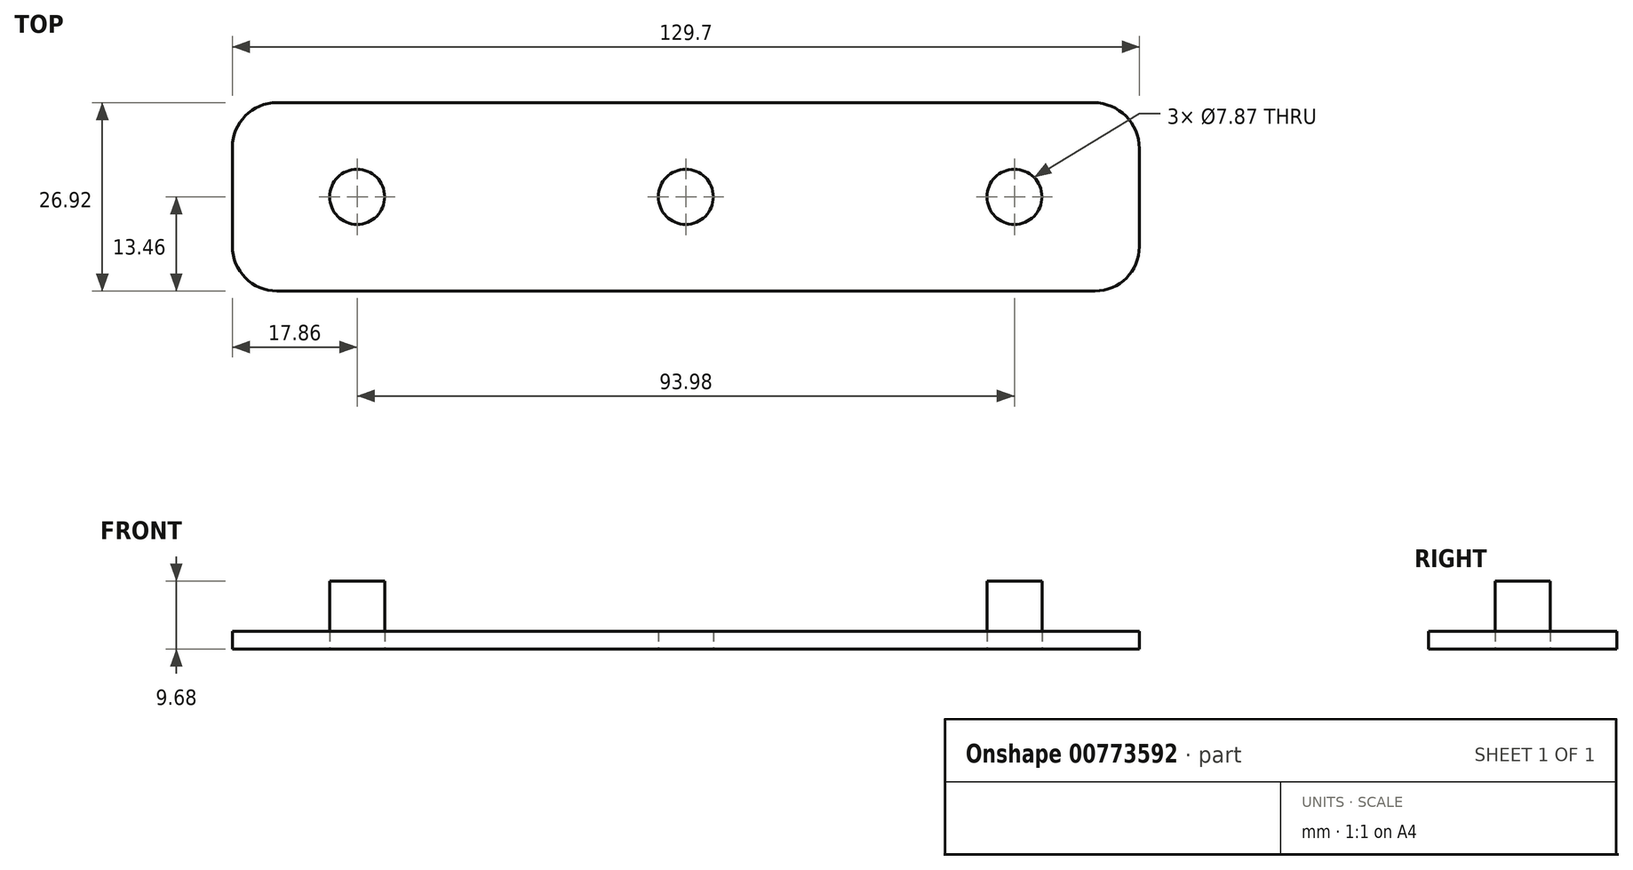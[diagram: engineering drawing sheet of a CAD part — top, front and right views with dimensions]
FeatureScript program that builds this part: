
annotation { "Feature Type Name" : "Feature", "Feature Type Description" : "" }
export const myFeature = defineFeature(function(context is Context, id is Id, definition is map)
    precondition{}
    {
        {
            var Q0;
            Q0=qCreatedBy(makeId("Top.planeOp"),FACE);
            var sketch = newSketch(context, id + "F0", { "sketchPlane" : qUnion([Q0])});
            skCircle(sketch, "E0", {"center": v(0, 0) * mm, "radius": 3.94 * mm});
            skCircle(sketch, "E1", {"center": v(47, 0) * mm, "radius": 3.94 * mm});
            skCircle(sketch, "E2", {"center": v(-47, 0) * mm, "radius": 3.94 * mm});
            skLineSegment(sketch, "E3", {"start": v(-58.44, 13.46) * mm, "end": v(58.3, 13.46) * mm});
            skLineSegment(sketch, "E4", {"start": v(0, 3.94) * mm, "end": v(0, 13.46) * mm});
            skLineSegment(sketch, "E5", {"start": v(0, -3.94) * mm, "end": v(0, -13.46) * mm});
            skLineSegment(sketch, "E6", {"start": v(-64.85, 7.06) * mm, "end": v(-64.85, -7.06) * mm});
            skLineSegment(sketch, "E7", {"start": v(-58.44, -13.46) * mm, "end": v(58.5, -13.46) * mm});
            skLineSegment(sketch, "E8", {"start": v(64.85, -7.11) * mm, "end": v(64.85, 6.9) * mm});
            skPoint(sketch, "E9.visualSharp", {"position": v(-64.85, -13.46) * mm});
            skArc(sketch, "E9.filletArc", {"start": v(-64.85, -7.06) * mm, "mid": v(-62.97, -11.59) * mm, "end": v(-58.44, -13.46) * mm});
            skPoint(sketch, "E10.visualSharp", {"position": v(-64.85, 13.46) * mm});
            skArc(sketch, "E10.filletArc", {"start": v(-58.44, 13.46) * mm, "mid": v(-62.97, 11.59) * mm, "end": v(-64.85, 7.06) * mm});
            skPoint(sketch, "E11.visualSharp", {"position": v(64.85, 13.46) * mm});
            skArc(sketch, "E11.filletArc", {"start": v(64.85, 6.9) * mm, "mid": v(62.93, 11.54) * mm, "end": v(58.3, 13.46) * mm});
            skPoint(sketch, "E12.visualSharp", {"position": v(64.85, -13.46) * mm});
            skArc(sketch, "E12.filletArc", {"start": v(58.5, -13.46) * mm, "mid": v(62.99, -11.6) * mm, "end": v(64.85, -7.11) * mm});
            skLineSegment(sketch, "E13", {"start": v(-47, 0) * mm, "end": v(0, 0) * mm});
            skLineSegment(sketch, "E14", {"start": v(47, 0) * mm, "end": v(0, 0) * mm});
            skLineSegment(sketch, "E15", {"start": v(-50.93, 0) * mm, "end": v(-64.85, 0) * mm});
            skSolve(sketch);
        }
        {
            var Q0;
            Q0=makeQuery(id+"F0.imprint","IMPRINT",FACE,{"disambiguationData":[TD([[makeQuery(id+"F0.imprint","IMPRINT",EDGE,{"derivedFrom":sQuery(id+"F0.wireOp",EDGE,"E1")}),1.0]])]});
            var Q1;
            {var subQ0=sQuery(id+"F0.wireOp",EDGE,"E2");var subQ1=makeQuery(id+"F0.imprint","INTERSECT",VERTEX,{"derivedFrom":[subQ0,sQuery(id+"F0.wireOp",EDGE,"E15")]});Q1=makeQuery(id+"F0.imprint","IMPRINT",FACE,{"disambiguationData":[TD([[makeQuery(id+"F0.imprint","IMPRINT",EDGE,{"disambiguationData":[TD([[subQ1,1.0]])],"derivedFrom":subQ0}),1.0]])]});}
            extrude(context, id + "F1", {"entities" : qUnion([Q0, Q1]), "depth" : 9.68 * mm, "offsetDistance" : 25.4 * mm});
        }
        {
            var Q0;
            Q0=makeQuery(id+"F0.imprint","IMPRINT",FACE,{"disambiguationData":[TD([[makeQuery(id+"F0.imprint","IMPRINT",EDGE,{"derivedFrom":sQuery(id+"F0.wireOp",EDGE,"E2")}),-1.0]])]});
            var Q1;
            Q1=makeQuery(id+"F0.imprint","IMPRINT",FACE,{"disambiguationData":[TD([[makeQuery(id+"F0.imprint","IMPRINT",EDGE,{"derivedFrom":sQuery(id+"F0.wireOp",EDGE,"E1")}),-1.0]])]});
            extrude(context, id + "F2", {"entities" : qUnion([Q0, Q1]), "depth" : 2.54 * mm, "offsetDistance" : 25.4 * mm});
        }
    });
